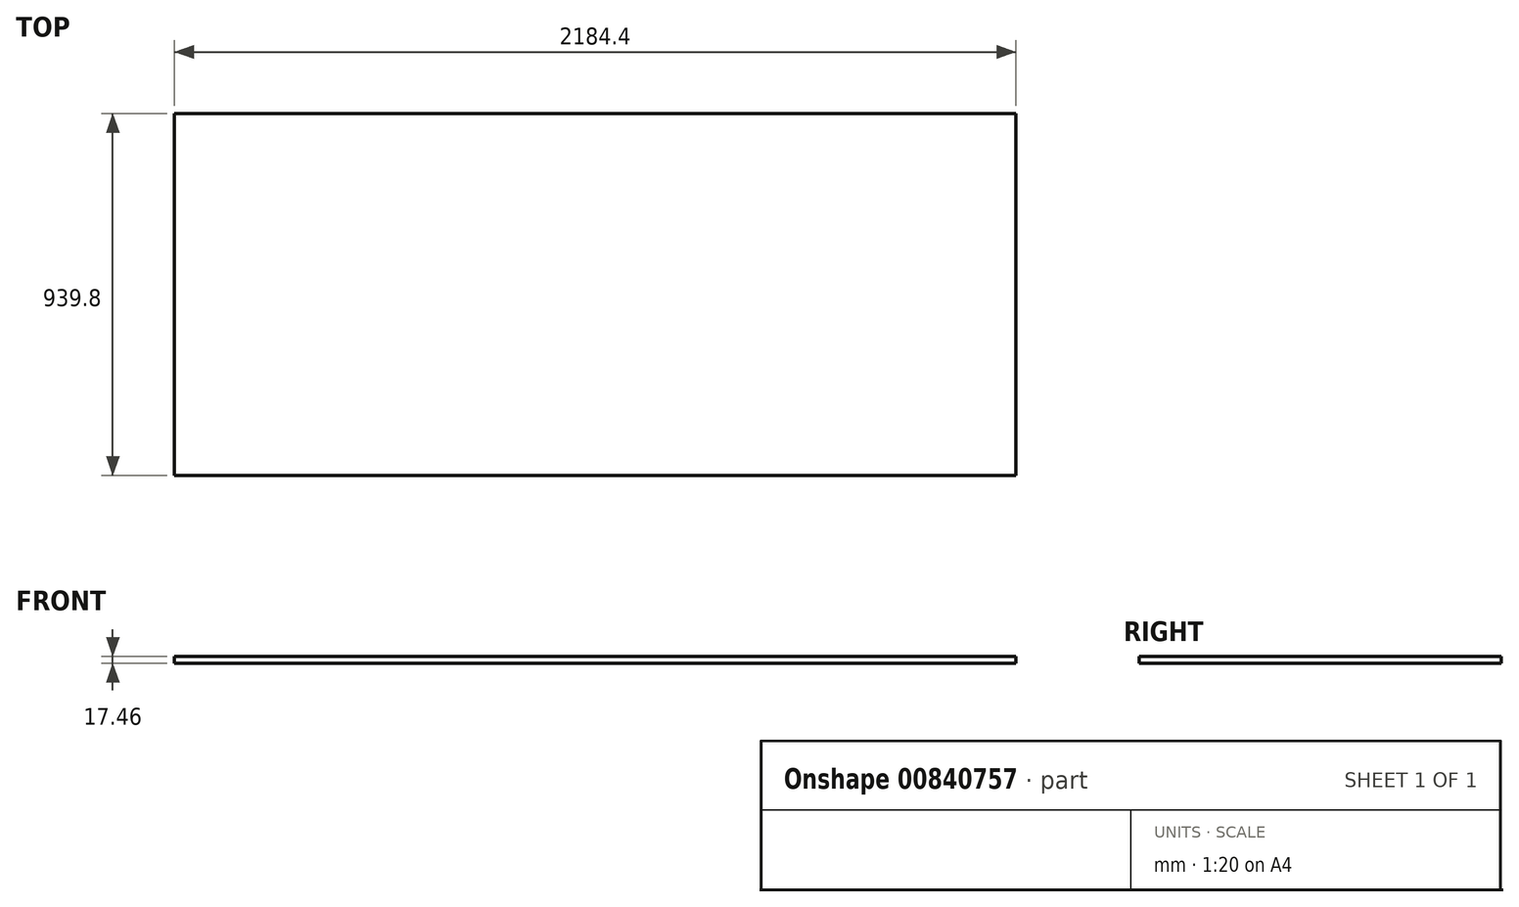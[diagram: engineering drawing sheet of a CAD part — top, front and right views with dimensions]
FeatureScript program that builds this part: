
annotation { "Feature Type Name" : "Feature", "Feature Type Description" : "" }
export const myFeature = defineFeature(function(context is Context, id is Id, definition is map)
    precondition{}
    {
        {
            var Q0;
            Q0=qCreatedBy(makeId("Top.planeOp"),FACE);
            var sketch = newSketch(context, id + "F0", { "sketchPlane" : qUnion([Q0])});
            skLineSegment(sketch, "E0.bottom", {"start": v(-2630.5, 939.8) * mm, "end": v(-446.1, 939.8) * mm});
            skLineSegment(sketch, "E0.top", {"start": v(-2630.5, 0) * mm, "end": v(-446.1, 0) * mm});
            skLineSegment(sketch, "E0.left", {"start": v(-2630.5, 939.8) * mm, "end": v(-2630.5, 0) * mm});
            skLineSegment(sketch, "E0.right", {"start": v(-446.1, 939.8) * mm, "end": v(-446.1, 0) * mm});
            skSolve(sketch);
        }
        {
            var Q0;
            Q0=makeQuery(id+"F0.imprint","IMPRINT",FACE,{"disambiguationData":[TD([[makeQuery(id+"F0.imprint","IMPRINT",EDGE,{"derivedFrom":sQuery(id+"F0.wireOp",EDGE,"E0.bottom")}),-1.0]])]});
            extrude(context, id + "F1", {"entities" : qUnion([Q0]), "depth" : 17.46 * mm, "offsetDistance" : 25.4 * mm});
        }
    });
